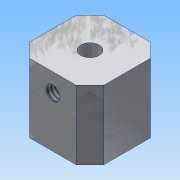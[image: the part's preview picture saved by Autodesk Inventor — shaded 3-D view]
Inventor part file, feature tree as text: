
AUTODESK INVENTOR PART (.ipt)
format: ipt  version: 2015 (Build 190159000, 159)  size: 117,760 bytes
history: native  units: mm
features: sketch x3, hole x2, extrude x1, chamfer x1, projected_geometry x1
ambient origin geometry x8: Origin, YZ Plane, XZ Plane, XY Plane, X Axis, Y Axis, Z Axis, Center Point
bodies: Volumenkörper1 (feature_tree)
feature tree (8):
  extrude  "Extrusion1"  Depth=7.5mm TaperAngle=0.0deg
  hole  "Bohrung1"  [1 undecoded]
  hole  "Bohrung2"  [1 undecoded]
  chamfer  "Fase1"  [1 undecoded]
  sketch  "Skizze1"  dims[d0=8.1mm d1=7.5mm d2=0.0mm]
  sketch  "Skizze3"  dims[d4=2.0mm d5=6.0mm d6=4.0mm d7=2.0mm d8=90.0deg d9=8.0mm d10=20.594885mm d11=2.0mm]
  sketch  "Skizze4"  dims[d12=1.567mm d13=4.0mm d14=4.0mm d15=2.0mm d16=90.0deg d17=8.0mm d18=20.594885mm d19=1.5mm d20=2.0mm d21=45.0deg]
  projected_geometry  "Projizierte Kontur1"
note: 3 required parameter values undecoded (feature->parameter linkage not recoverable at this tier; creation-order binding heuristic only, values carry confidence <= 0.55)
